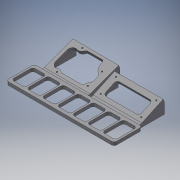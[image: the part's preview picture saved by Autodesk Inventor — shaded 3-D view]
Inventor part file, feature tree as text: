
AUTODESK INVENTOR PART (.ipt)
format: ipt  version: 2017 (Build 210142000, 142)  size: 322,048 bytes
history: native  units: mm
features: sketch x11, extrude x7, other x5, reference x4, pattern_linear x3, hole x2, fillet x2, mirror x1
ambient origin geometry x8: Origin, YZ Plane, XZ Plane, XY Plane, X Axis, Y Axis, Z Axis, Center Point
bodies: Solid1 (feature_tree)
feature tree (35):
  extrude  "Extrusion1"  Depth=200.0mm
  other  "Bend Part1"
  hole  "Hole2"  [1 undecoded]
  extrude  "Extrusion2"  Depth=15.0mm
  other  "Bend Part2"
  hole  "Hole3"  [1 undecoded]
  extrude  "Extrusion3"  Depth=6.0mm
  fillet  "Fillet1"  Radius=6.0mm
  pattern_linear  "Rectangular Pattern1"  Spacing1=15.0mm  [1 undecoded]
  mirror  "Mirror1"
  extrude  "Extrusion4"  Depth=40.0mm
  extrude  "Extrusion5"  Depth=10.0mm TaperAngle=0.0deg
  extrude  "Extrusion6"  Depth=40.0mm
  pattern_linear  "Rectangular Pattern2"  Spacing1=5.0mm  [1 undecoded]
  extrude  "Extrusion7"  Depth=5.0mm
  pattern_linear  "Rectangular Pattern3"  Spacing1=6.0mm  [1 undecoded]
  fillet  "Fillet2"  Radius=5.0mm
  sketch  "Sketch1"  dims[d0=6.0mm d1=0.0mm d2=200.0mm]
  sketch  "Sketch3"  dims[d3=52.0mm d6=85.0mm]
  sketch  "Sketch4"  dims[d7=60.0mm d8=15.0mm]
  reference  "Reference5"
  reference  "Reference6"
  reference  "Reference7"
  reference  "Reference8"
  sketch  "Sketch5"  dims[d16=10.0mm d17=3.490659mm]
  sketch  "Sketch6"  dims[d18=2.5mm d19=6.0mm d20=4.0mm d21=2.0mm d22=90.0deg d23=8.0mm d24=20.594885mm d25=90.0mm]
  sketch  "Sketch7"  dims[d26=5.0mm d27=48.0mm d28=6.0mm d29=0.0mm]
  sketch  "Sketch8"  dims[d30=10.0mm d31=4.363323mm]
  sketch  "Sketch9"  dims[d32=75.0mm]
  sketch  "Sketch10"  dims[d33=31.0mm]
  sketch  "Sketch11"  dims[d34=6.0mm]
  sketch  "Sketch12"  dims[d35=8.0mm d36=2.5mm d37=6.0mm d38=4.0mm d39=2.0mm d40=90.0deg d41=8.0mm d42=20.594885mm d43=15.0mm d44=40.0mm d45=10.0mm d46=0.0mm d47=40.0mm d49=20.0mm d50=5.0mm d51=5.0mm d52=6.0mm d53=0.0mm d54=5.0mm d55=6.0mm d56=0.0mm d57=4.0mm d58=0.0mm d59=20.0mm d61=86.0mm d62=4.0mm d63=0.0mm d64=20.0mm d66=81.0mm d67=5.0mm]
  other  "<userpath>\Google Drive\Metal Class Projetos\Diversos\Montagem_Arduino.iam"
  other  "Montagem_Arduino.iam"
  other  "ArduinoUNO :2"
note: 5 required parameter values undecoded (feature->parameter linkage not recoverable at this tier; creation-order binding heuristic only, values carry confidence <= 0.55)
